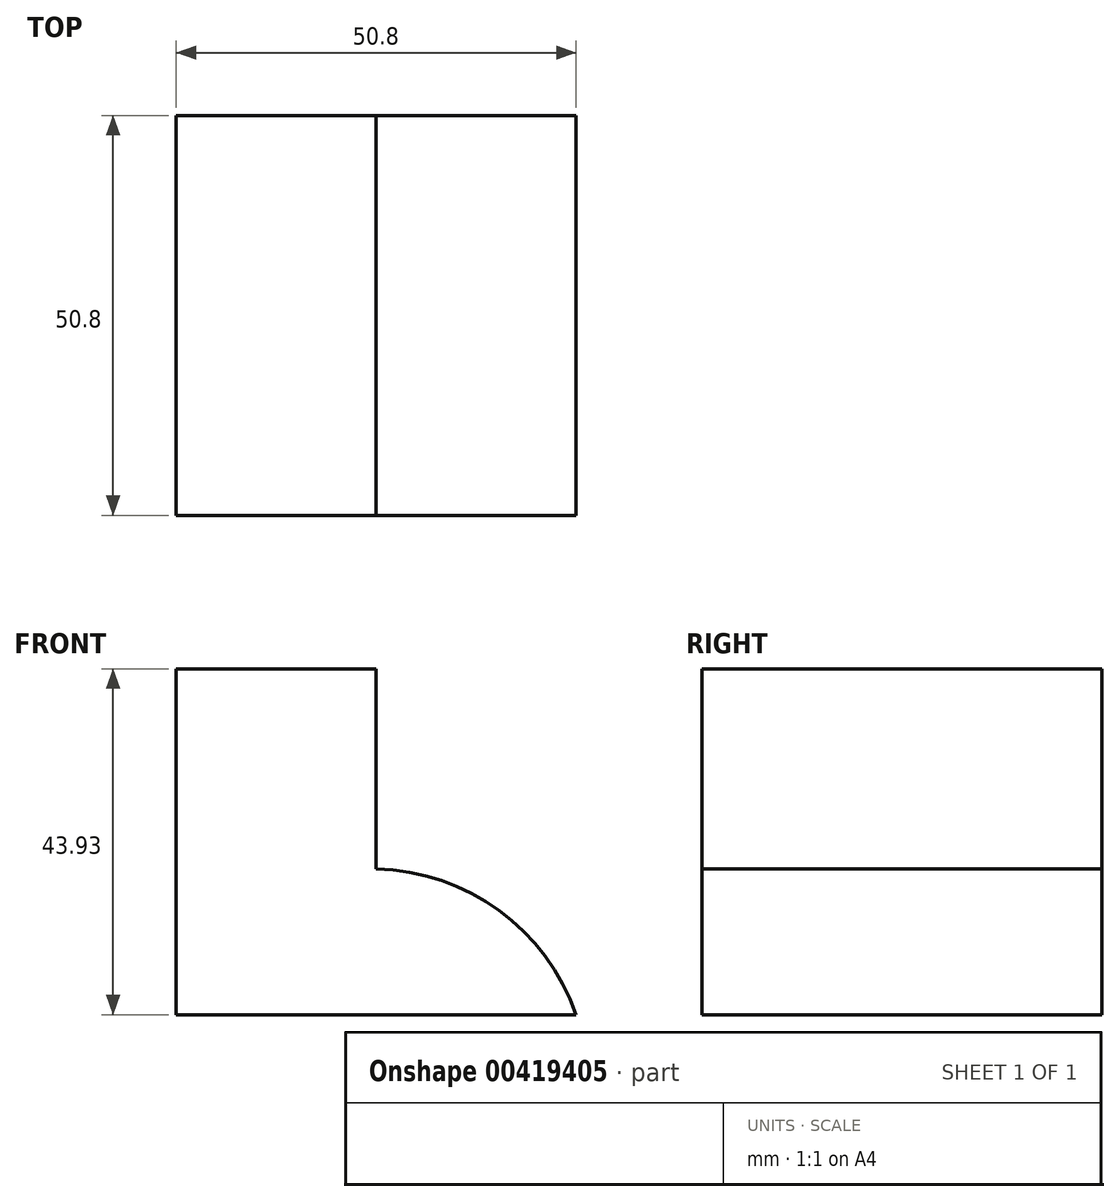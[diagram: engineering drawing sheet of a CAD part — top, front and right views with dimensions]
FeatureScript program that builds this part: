
annotation { "Feature Type Name" : "Feature", "Feature Type Description" : "" }
export const myFeature = defineFeature(function(context is Context, id is Id, definition is map)
    precondition{}
    {
        {
            var Q0;
            Q0=qCreatedBy(makeId("Front.planeOp"),FACE);
            var sketch = newSketch(context, id + "F0", { "sketchPlane" : qUnion([Q0])});
            skLineSegment(sketch, "E0", {"start": v(0, 0) * mm, "end": v(-50.8, 0) * mm});
            skLineSegment(sketch, "E1", {"start": v(-50.8, 0) * mm, "end": v(-50.8, 43.93) * mm});
            skLineSegment(sketch, "E2", {"start": v(-50.8, 43.93) * mm, "end": v(-25.4, 43.93) * mm});
            skLineSegment(sketch, "E3", {"start": v(-25.4, 43.93) * mm, "end": v(-25.4, 18.53) * mm});
            skArc(sketch, "E4", {"start": v(0, 0) * mm, "mid": v(-9.8, 13.23) * mm, "end": v(-25.4, 18.53) * mm});
            skSolve(sketch);
        }
        {
            var Q0;
            Q0 = qSketchRegion(id + "F0", true);
            extrude(context, id + "F1", {"entities" : qUnion([Q0]), "depth" : 50.8 * mm});
        }
    });
